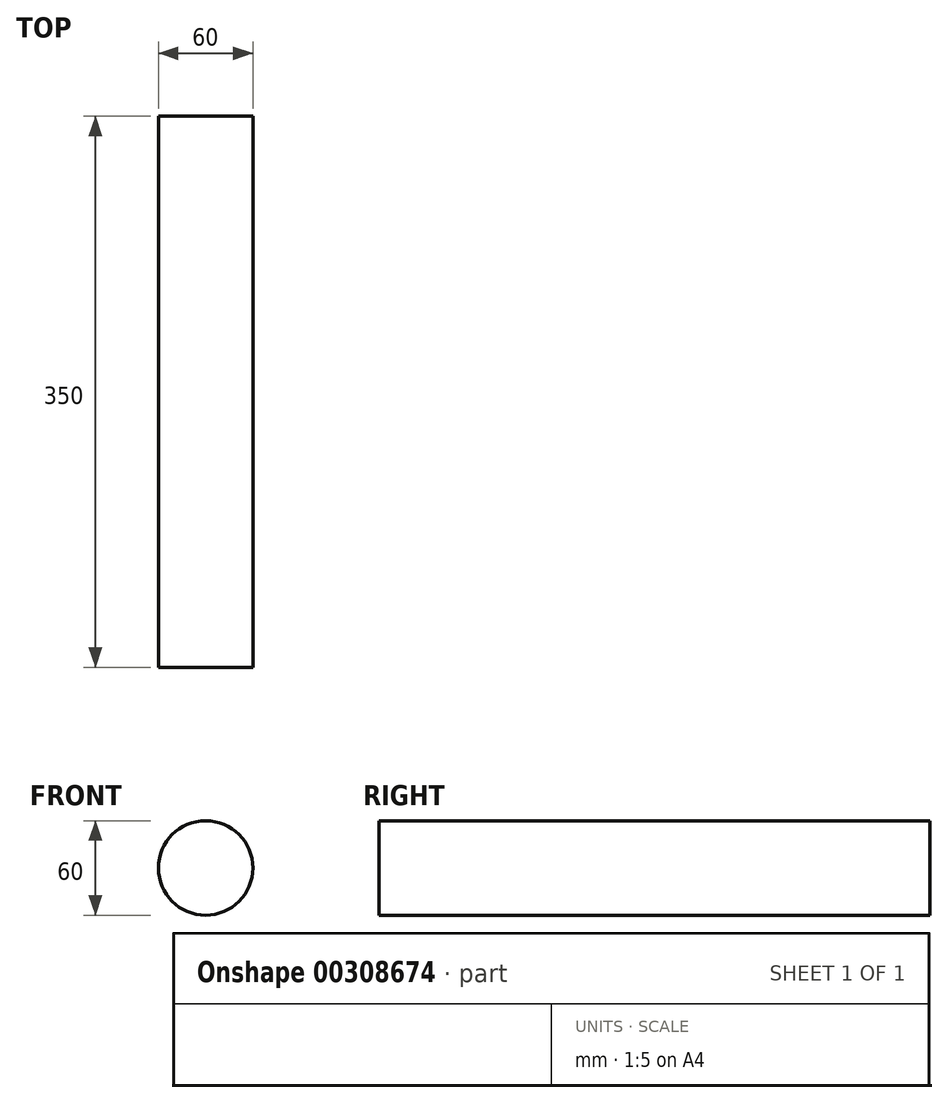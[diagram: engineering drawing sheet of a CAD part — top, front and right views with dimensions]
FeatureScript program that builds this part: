
annotation { "Feature Type Name" : "Feature", "Feature Type Description" : "" }
export const myFeature = defineFeature(function(context is Context, id is Id, definition is map)
    precondition{}
    {
        {
            var Q0;
            Q0=qCreatedBy(makeId("Front.planeOp"),FACE);
            var sketch = newSketch(context, id + "F0", { "sketchPlane" : qUnion([Q0])});
            skCircle(sketch, "E0", {"center": v(0, 0) * mm, "radius": 30 * mm});
            skSolve(sketch);
        }
        {
            var Q0;
            Q0=makeQuery(id+"F0.imprint","IMPRINT",FACE,{"disambiguationData":[TD([[makeQuery(id+"F0.imprint","IMPRINT",EDGE,{"derivedFrom":sQuery(id+"F0.wireOp",EDGE,"E0")}),1.0]])]});
            var Q1;
            Q1=sQuery(id+"F0.wireOp",EDGE,"E0");
            extrude(context, id + "F1", {"entities" : qUnion([Q0]), "surfaceEntities" : qUnion([Q1]), "depth" : 350 * mm});
        }
    });
